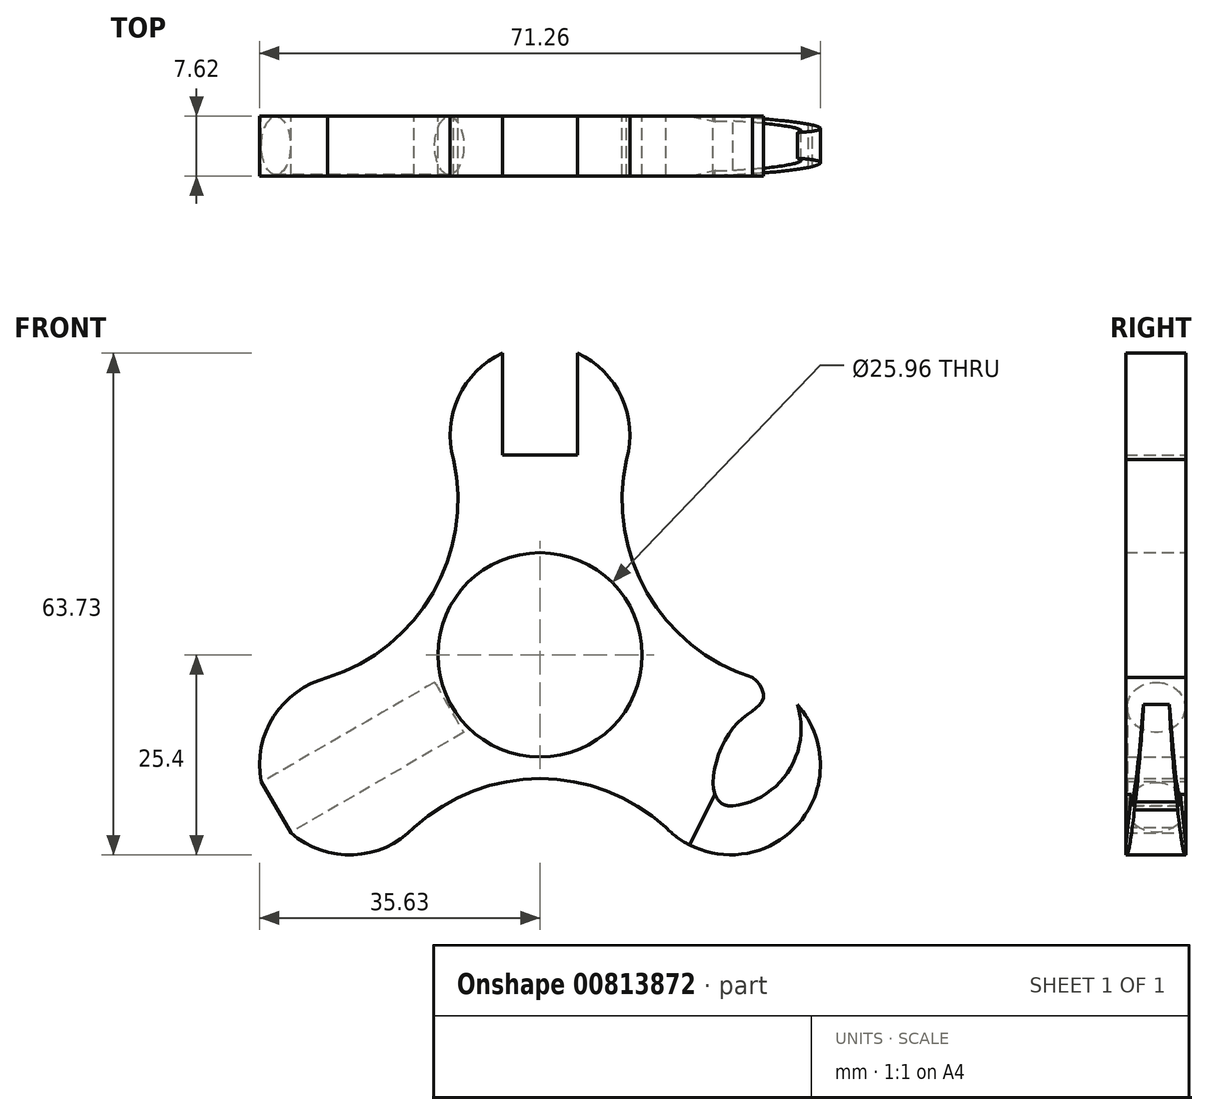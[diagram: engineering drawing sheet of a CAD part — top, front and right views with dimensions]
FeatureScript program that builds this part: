
annotation { "Feature Type Name" : "Feature", "Feature Type Description" : "" }
export const myFeature = defineFeature(function(context is Context, id is Id, definition is map)
    precondition{}
    {
        {
            var Q0;
            Q0=qCreatedBy(makeId("Front.planeOp"),FACE);
            var sketch = newSketch(context, id + "F0", { "sketchPlane" : qUnion([Q0])});
            skCircle(sketch, "E0", {"center": v(0, 0) * mm, "radius": 25.4 * mm, "construction": true});
            skLineSegment(sketch, "E1", {"start": v(0, 0) * mm, "end": v(0, 25.4) * mm});
            skLineSegment(sketch, "E2.1.0", {"start": v(0, 0) * mm, "end": v(-22, -12.7) * mm});
            skLineSegment(sketch, "E2.2.0", {"start": v(0, 0) * mm, "end": v(22, -12.7) * mm});
            skCircle(sketch, "E3", {"center": v(0, 0) * mm, "radius": 12.98 * mm});
            skLineSegment(sketch, "E4", {"start": v(0, 0) * mm, "end": v(-42.35, -24.45) * mm, "construction": true});
            skLineSegment(sketch, "E5.1.0", {"start": v(0, 0) * mm, "end": v(42.35, -24.45) * mm, "construction": true});
            skLineSegment(sketch, "E5.2.0", {"start": v(0, 0) * mm, "end": v(0, 48.9) * mm, "construction": true});
            skPoint(sketch, "E6", {"position": v(-24.2, -13.97) * mm});
            skArc(sketch, "E7", {"start": v(-31.65, -22.63) * mm, "mid": v(-14.3, -8.25) * mm, "end": v(-35.43, -16.1) * mm});
            skPoint(sketch, "E8", {"position": v(-16, -21.94) * mm});
            skLineSegment(sketch, "E9", {"start": v(-16, -21.94) * mm, "end": v(16, -21.94) * mm, "construction": true});
            skCircle(sketch, "E10.1.0", {"center": v(24.2, -13.97) * mm, "radius": 11.43 * mm});
            skArc(sketch, "E10.2.0", {"start": v(-4.76, 38.33) * mm, "mid": v(0, 16.51) * mm, "end": v(4.76, 38.33) * mm});
            skArc(sketch, "E11", {"start": v(16, -21.94) * mm, "mid": v(0, -15.72) * mm, "end": v(-16, -21.94) * mm});
            skArc(sketch, "E12.1.0", {"start": v(11, 24.83) * mm, "mid": v(13.61, 7.86) * mm, "end": v(27, -2.89) * mm});
            skArc(sketch, "E12.2.0", {"start": v(-27, -2.89) * mm, "mid": v(-13.61, 7.86) * mm, "end": v(-11, 24.83) * mm});
            skLineSegment(sketch, "E13", {"start": v(-11.14, 25.4) * mm, "end": v(11.14, 25.4) * mm, "construction": true});
            skLineSegment(sketch, "E14", {"start": v(-4.76, 25.4) * mm, "end": v(-4.76, 38.33) * mm});
            skLineSegment(sketch, "E15", {"start": v(4.76, 25.4) * mm, "end": v(4.76, 38.33) * mm});
            skPoint(sketch, "E16", {"position": v(-4.76, 25.4) * mm});
            skPoint(sketch, "E17", {"position": v(4.76, 25.4) * mm});
            skLineSegment(sketch, "E18", {"start": v(-4.76, 25.4) * mm, "end": v(4.76, 25.4) * mm});
            skPoint(sketch, "E19", {"position": v(-4.76, 38.33) * mm});
            skPoint(sketch, "E20", {"position": v(4.76, 38.33) * mm});
            skLineSegment(sketch, "E21", {"start": v(-35.43, -16.1) * mm, "end": v(-31.65, -22.63) * mm});
            skArc(sketch, "E22", {"start": v(24.54, -19.21) * mm, "mid": v(31.64, -14.67) * mm, "end": v(32.68, -6.3) * mm});
            skFitSpline(sketch, "E23", {"points": [v(24.54, -19.21) * mm, v(22, -16.25) * mm, v(25.07, -8.66) * mm, v(28.3, -5.72) * mm, v(27, -2.89) * mm], "startDerivative": vector(-24.34, -0.66) * mm, "endDerivative": vector(-15.21, 11.09) * mm});
            skLineSegment(sketch, "E24", {"start": v(34.1, -19.69) * mm, "end": v(29.54, -17.05) * mm});
            skLineSegment(sketch, "E25", {"start": v(32.68, -6.3) * mm, "end": v(40.15, -7.88) * mm});
            skLineSegment(sketch, "E26", {"start": v(40.15, -7.88) * mm, "end": v(34.1, -19.69) * mm});
            skSolve(sketch);
        }
        {
            var Q0;
            {var subQ5=sQuery(id+"F0.wireOp",EDGE,"E24");Q0=makeQuery(id+"F0.imprint","IMPRINT",FACE,{"disambiguationData":[TD([[makeQuery(id+"F0.imprint","IMPRINT",EDGE,{"derivedFrom":subQ5}),-1.0]])]});}
            var Q1;
            {var subQ0=sQuery(id+"F0.wireOp",EDGE,"E23");Q1=makeQuery(id+"F0.imprint","IMPRINT",FACE,{"disambiguationData":[TD([[makeQuery(id+"F0.imprint","IMPRINT",EDGE,{"derivedFrom":subQ0}),1.0]])]});}
            var Q2;
            {var subQ5=sQuery(id+"F0.wireOp",EDGE,"E11");Q2=makeQuery(id+"F0.imprint","IMPRINT",FACE,{"disambiguationData":[TD([[makeQuery(id+"F0.imprint","IMPRINT",EDGE,{"derivedFrom":subQ5}),-1.0]])]});}
            var Q3;
            {var subQ4=sQuery(id+"F0.wireOp",EDGE,"E14");Q3=makeQuery(id+"F0.imprint","IMPRINT",FACE,{"disambiguationData":[TD([[makeQuery(id+"F0.imprint","IMPRINT",EDGE,{"derivedFrom":subQ4}),1.0]])]});}
            var Q4;
            {var subQ0=sQuery(id+"F0.wireOp",EDGE,"E12.1.0");Q4=makeQuery(id+"F0.imprint","IMPRINT",FACE,{"disambiguationData":[TD([[makeQuery(id+"F0.imprint","IMPRINT",EDGE,{"derivedFrom":subQ0}),-1.0]])]});}
            var Q5;
            {var subQ0=sQuery(id+"F0.wireOp",EDGE,"E21");Q5=makeQuery(id+"F0.imprint","IMPRINT",FACE,{"disambiguationData":[TD([[makeQuery(id+"F0.imprint","IMPRINT",EDGE,{"derivedFrom":subQ0}),1.0]])]});}
            var Q6;
            {var subQ0=sQuery(id+"F0.wireOp",EDGE,"E12.2.0");Q6=makeQuery(id+"F0.imprint","IMPRINT",FACE,{"disambiguationData":[TD([[makeQuery(id+"F0.imprint","IMPRINT",EDGE,{"derivedFrom":subQ0}),-1.0]])]});}
            var Q7;
            {var subQ0=sQuery(id+"F0.wireOp",EDGE,"E15");Q7=makeQuery(id+"F0.imprint","IMPRINT",FACE,{"disambiguationData":[TD([[makeQuery(id+"F0.imprint","IMPRINT",EDGE,{"derivedFrom":subQ0}),-1.0]])]});}
            var Q8;
            Q8 = qSketchRegion(id + "F2", true);
            var Q9;
            Q9 = qSketchRegion(id + "F4", true);
            extrude(context, id + "F1", {"entities" : qUnion([Q0, Q1, Q2, Q3, Q4, Q5, Q6, Q7, Q8, Q9]), "depth" : 7.62 * mm, "offsetDistance" : 25.4 * mm});
        }
        {
            var Q0;
            Q0=makeQuery(id+"F1.opExtrude","SWEPT_FACE",FACE,{"disambiguationData":[OSD([sQuery(id+"F0.wireOp",EDGE,"E21")])]});
            var sketch = newSketch(context, id + "F2", { "sketchPlane" : qUnion([Q0])});
            skCircle(sketch, "E27", {"center": v(3.76, 0) * mm, "radius": 3.68 * mm});
            skSolve(sketch);
        }
        {
            var Q0;
            Q0=makeQuery(id+"F2.imprint","IMPRINT",FACE,{"disambiguationData":[TD([[makeQuery(id+"F2.imprint","IMPRINT",EDGE,{"derivedFrom":sQuery(id+"F2.wireOp",EDGE,"E27")}),1.0]])]});
            extrude(context, id + "F3", {"entities" : qUnion([Q0]), "operationType" : NewBodyOperationType.REMOVE, "oppositeDirection" : true, "depth" : 25.4 * mm, "offsetDistance" : 25.4 * mm});
        }
        {
            var Q0;
            Q0=makeQuery(id+"F1.opExtrude","SWEPT_FACE",FACE,{"disambiguationData":[OSD([sQuery(id+"F0.wireOp",EDGE,"E26")])]});
            var sketch = newSketch(context, id + "F4", { "sketchPlane" : qUnion([Q0])});
            skLineSegment(sketch, "E28.0", {"start": v(-7.62, 9.3) * mm, "end": v(0, 9.3) * mm});
            skLineSegment(sketch, "E29", {"start": v(0, -12.82) * mm, "end": v(-7.62, -12.82) * mm});
            skLineSegment(sketch, "E30", {"start": v(0, -12.82) * mm, "end": v(-2.1, 9.3) * mm});
            skLineSegment(sketch, "E31", {"start": v(-7.62, -12.82) * mm, "end": v(-5.37, 9.3) * mm});
            skLineSegment(sketch, "E32", {"start": v(-7.62, -12.82) * mm, "end": v(-7.62, 9.3) * mm});
            skLineSegment(sketch, "E33", {"start": v(0, -12.82) * mm, "end": v(0, 9.3) * mm});
            skSolve(sketch);
        }
        {
            var Q0;
            {var subQ0=sQuery(id+"F4.wireOp",EDGE,"E32");var subQ1=sQuery(id+"F4.wireOp",EDGE,"E31");var subQ2=makeQuery(id+"F4.imprint","INTERSECT",VERTEX,{"derivedFrom":[sQuery(id+"F4.wireOp",EDGE,"E29"),subQ1,subQ0]});Q0=makeQuery(id+"F4.imprint","IMPRINT",FACE,{"disambiguationData":[TD([[makeQuery(id+"F4.imprint","IMPRINT",EDGE,{"disambiguationData":[TD([[subQ2,-1.0]])],"derivedFrom":subQ1}),1.0]])]});}
            var Q1;
            {var subQ0=sQuery(id+"F4.wireOp",EDGE,"E31");var subQ1=sQuery(id+"F0.wireOp",EDGE,"E26");var subQ2=sQuery(id+"F0.wireOp",EDGE,"E10.1.0");var subQ5=makeQuery(id+"F1.opExtrude","SWEPT_EDGE",EDGE,{"disambiguationData":[OSD([subQ2,subQ1])]});var subQ6=makeQuery(id+"F4.imprint","INTERSECT",VERTEX,{"derivedFrom":[subQ5,subQ0]});Q1=makeQuery(id+"F4.imprint","IMPRINT",FACE,{"disambiguationData":[TD([[makeQuery(id+"F4.imprint","IMPRINT",EDGE,{"disambiguationData":[TD([[subQ6,1.0]])],"derivedFrom":subQ0}),1.0]])]});}
            var Q2;
            {var subQ0=sQuery(id+"F4.wireOp",EDGE,"E32");var subQ1=sQuery(id+"F4.wireOp",EDGE,"E28.0");var subQ2=makeQuery(id+"F4.imprint","INTERSECT",VERTEX,{"derivedFrom":[subQ1,subQ0]});Q2=makeQuery(id+"F4.imprint","IMPRINT",FACE,{"disambiguationData":[TD([[makeQuery(id+"F4.imprint","IMPRINT",EDGE,{"disambiguationData":[TD([[subQ2,-1.0]])],"derivedFrom":subQ1}),-1.0]])]});}
            var Q3;
            {var subQ0=sQuery(id+"F4.wireOp",EDGE,"E33");var subQ1=sQuery(id+"F4.wireOp",EDGE,"E28.0");var subQ2=makeQuery(id+"F4.imprint","INTERSECT",VERTEX,{"derivedFrom":[subQ1,subQ0]});Q3=makeQuery(id+"F4.imprint","IMPRINT",FACE,{"disambiguationData":[TD([[makeQuery(id+"F4.imprint","IMPRINT",EDGE,{"disambiguationData":[TD([[subQ2,1.0]])],"derivedFrom":subQ1}),-1.0]])]});}
            var Q4;
            {var subQ0=sQuery(id+"F4.wireOp",EDGE,"E30");var subQ1=sQuery(id+"F0.wireOp",EDGE,"E26");var subQ2=sQuery(id+"F0.wireOp",EDGE,"E10.1.0");var subQ5=makeQuery(id+"F1.opExtrude","SWEPT_EDGE",EDGE,{"disambiguationData":[OSD([subQ2,subQ1])]});var subQ6=makeQuery(id+"F4.imprint","INTERSECT",VERTEX,{"derivedFrom":[subQ5,subQ0]});Q4=makeQuery(id+"F4.imprint","IMPRINT",FACE,{"disambiguationData":[TD([[makeQuery(id+"F4.imprint","IMPRINT",EDGE,{"disambiguationData":[TD([[subQ6,1.0]])],"derivedFrom":subQ0}),-1.0]])]});}
            var Q5;
            {var subQ0=sQuery(id+"F4.wireOp",EDGE,"E33");var subQ1=sQuery(id+"F4.wireOp",EDGE,"E30");var subQ2=makeQuery(id+"F4.imprint","INTERSECT",VERTEX,{"derivedFrom":[sQuery(id+"F4.wireOp",EDGE,"E29"),subQ1,subQ0]});Q5=makeQuery(id+"F4.imprint","IMPRINT",FACE,{"disambiguationData":[TD([[makeQuery(id+"F4.imprint","IMPRINT",EDGE,{"disambiguationData":[TD([[subQ2,-1.0]])],"derivedFrom":subQ1}),-1.0]])]});}
            extrude(context, id + "F5", {"entities" : qUnion([Q0, Q1, Q2, Q3, Q4, Q5]), "operationType" : NewBodyOperationType.REMOVE, "oppositeDirection" : true, "depth" : 11.43 * mm, "offsetDistance" : 25.4 * mm});
        }
    });
